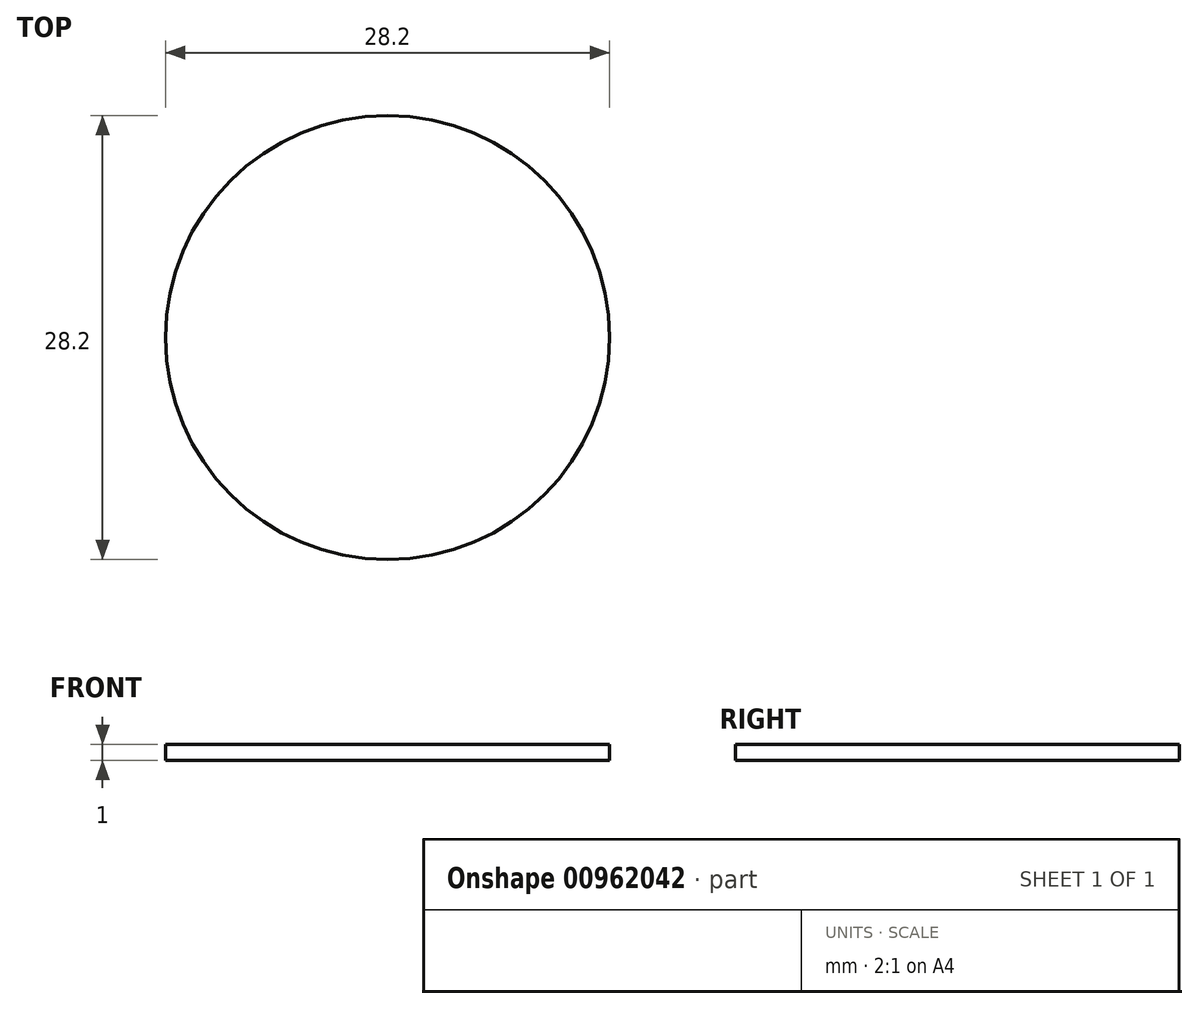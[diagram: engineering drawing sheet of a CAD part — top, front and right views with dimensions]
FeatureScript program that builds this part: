
annotation { "Feature Type Name" : "Feature", "Feature Type Description" : "" }
export const myFeature = defineFeature(function(context is Context, id is Id, definition is map)
    precondition{}
    {
        {
            assignVariable(context, id + "F0", {"variableType" : VariableType.LENGTH, "name" : "height", "lengthValue" : 1 * mm});
        }
        {
            var Q0;
            Q0=qCreatedBy(makeId("Top.planeOp"),FACE);
            var sketch = newSketch(context, id + "F1", { "sketchPlane" : qUnion([Q0])});
            skCircle(sketch, "E0", {"center": v(0, 0) * mm, "radius": 14.1 * mm});
            skSolve(sketch);
        }
        {
            var Q0;
            Q0=makeQuery(id+"F1.imprint","IMPRINT",FACE,{"disambiguationData":[TD([[makeQuery(id+"F1.imprint","IMPRINT",EDGE,{"derivedFrom":sQuery(id+"F1.wireOp",EDGE,"E0")}),1.0]])]});
            extrude(context, id + "F2", {"entities" : qUnion([Q0]), "depth" : getVariable(context, 'height'), "offsetDistance" : 25 * mm});
        }
    });
